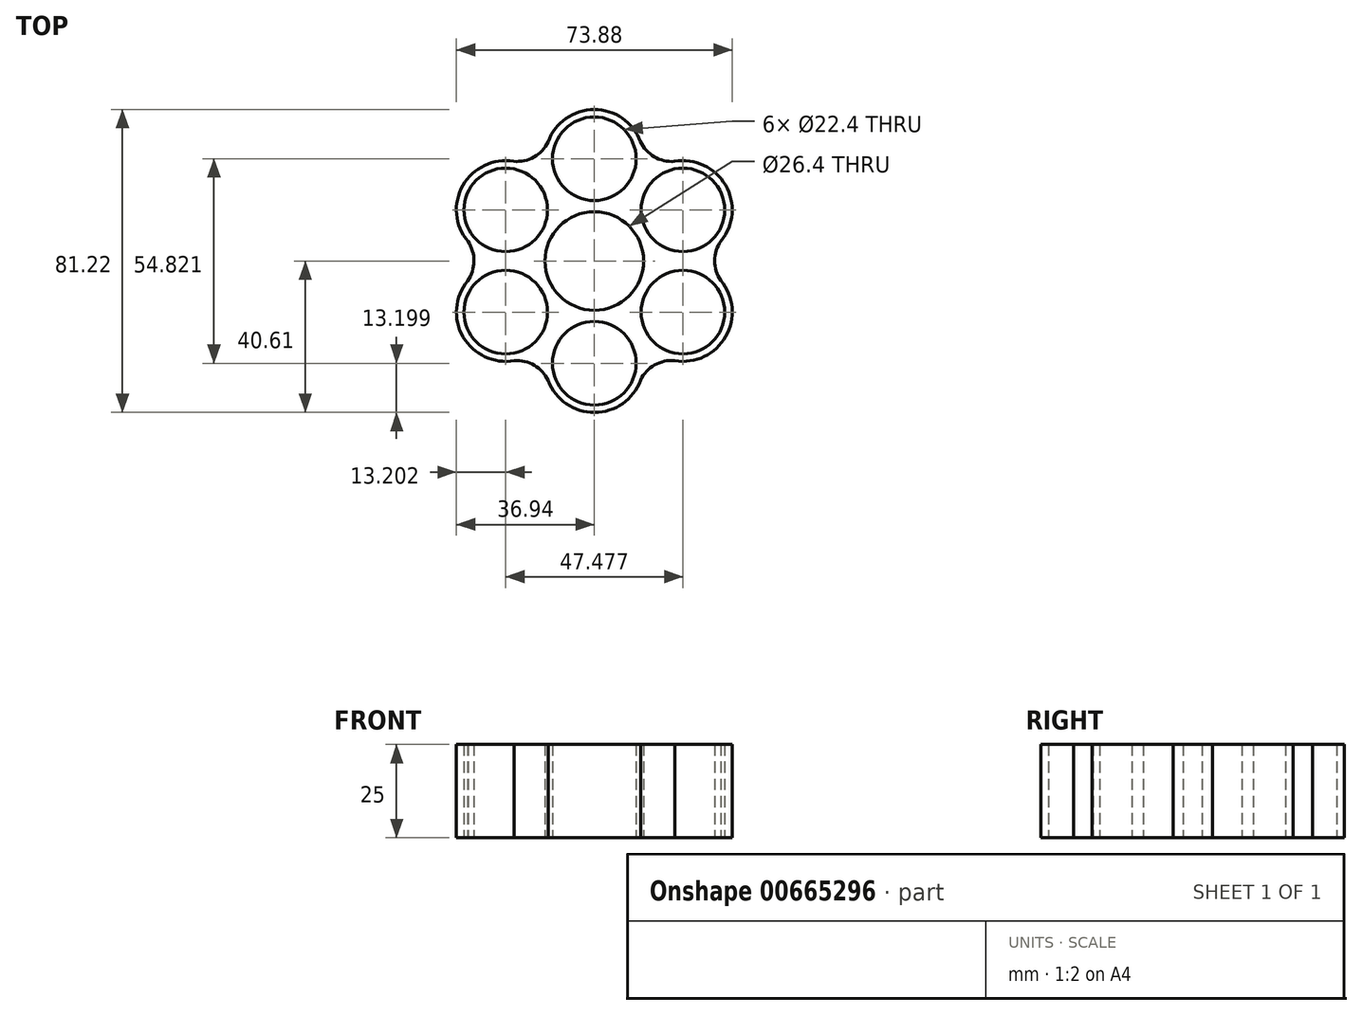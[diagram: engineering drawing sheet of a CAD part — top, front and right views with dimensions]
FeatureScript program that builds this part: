
annotation { "Feature Type Name" : "Feature", "Feature Type Description" : "" }
export const myFeature = defineFeature(function(context is Context, id is Id, definition is map)
    precondition{}
    {
        {
            var Q0;
            Q0=qCreatedBy(makeId("Top.planeOp"),FACE);
            var sketch = newSketch(context, id + "F0", { "sketchPlane" : qUnion([Q0])});
            skCircle(sketch, "E0", {"center": v(0, 0) * mm, "radius": 11.2 * mm});
            skCircle(sketch, "E1", {"center": v(0, 0) * mm, "radius": 13.2 * mm});
            skCircle(sketch, "E2", {"center": v(0, 27.41) * mm, "radius": 11.2 * mm});
            skCircle(sketch, "E3", {"center": v(0, 27.41) * mm, "radius": 13.2 * mm});
            skCircle(sketch, "E4.1.0", {"center": v(-23.74, 13.7) * mm, "radius": 11.2 * mm});
            skCircle(sketch, "E4.1.1", {"center": v(-23.74, 13.7) * mm, "radius": 13.2 * mm});
            skCircle(sketch, "E4.2.0", {"center": v(-23.74, -13.7) * mm, "radius": 11.2 * mm});
            skCircle(sketch, "E4.2.1", {"center": v(-23.74, -13.7) * mm, "radius": 13.2 * mm});
            skCircle(sketch, "E4.3.0", {"center": v(0, -27.41) * mm, "radius": 11.2 * mm});
            skCircle(sketch, "E4.3.1", {"center": v(0, -27.41) * mm, "radius": 13.2 * mm});
            skCircle(sketch, "E4.4.0", {"center": v(23.74, -13.7) * mm, "radius": 11.2 * mm});
            skCircle(sketch, "E4.4.1", {"center": v(23.74, -13.7) * mm, "radius": 13.2 * mm});
            skCircle(sketch, "E4.5.0", {"center": v(23.74, 13.7) * mm, "radius": 11.2 * mm});
            skCircle(sketch, "E4.5.1", {"center": v(23.74, 13.7) * mm, "radius": 13.2 * mm});
            skArc(sketch, "E5", {"start": v(-34.37, -5.89) * mm, "mid": v(-32.23, 0.07) * mm, "end": v(-34.46, 6) * mm});
            skArc(sketch, "E6.1.0", {"start": v(-12.09, -32.71) * mm, "mid": v(-16.18, -27.87) * mm, "end": v(-22.42, -26.84) * mm});
            skArc(sketch, "E6.2.0", {"start": v(22.28, -26.82) * mm, "mid": v(16.05, -27.95) * mm, "end": v(12.03, -32.84) * mm});
            skArc(sketch, "E6.3.0", {"start": v(34.37, 5.89) * mm, "mid": v(32.23, -0.07) * mm, "end": v(34.46, -6) * mm});
            skArc(sketch, "E6.4.0", {"start": v(12.09, 32.71) * mm, "mid": v(16.18, 27.87) * mm, "end": v(22.42, 26.84) * mm});
            skArc(sketch, "E6.5.0", {"start": v(-22.28, 26.82) * mm, "mid": v(-16.05, 27.95) * mm, "end": v(-12.03, 32.84) * mm});
            skSolve(sketch);
        }
        {
            var Q0;
            Q0 = qSketchRegion(id + "F0", true);
            extrude(context, id + "F1", {"entities" : qUnion([Q0]), "depth" : 25 * mm, "offsetDistance" : 25 * mm});
        }
    });
